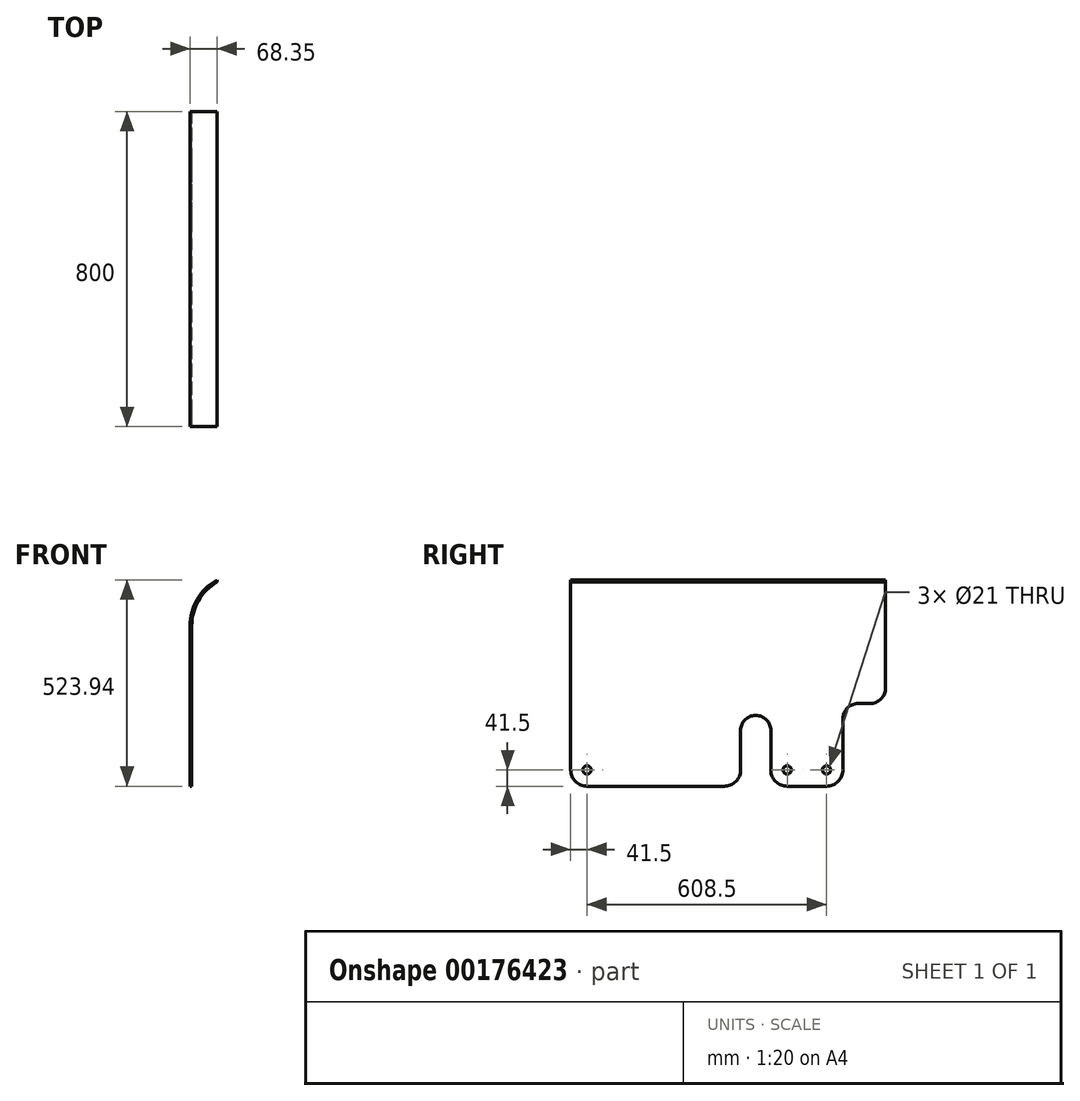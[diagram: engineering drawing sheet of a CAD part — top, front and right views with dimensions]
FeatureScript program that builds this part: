
annotation { "Feature Type Name" : "Feature", "Feature Type Description" : "" }
export const myFeature = defineFeature(function(context is Context, id is Id, definition is map)
    precondition{}
    {
        {
            var Q0;
            Q0=qCreatedBy(makeId("Front.planeOp"),FACE);
            var sketch = newSketch(context, id + "F0", { "sketchPlane" : qUnion([Q0])});
            skArc(sketch, "E0", {"start": v(68.35, 116.64) * mm, "mid": v(18.35, 67.6) * mm, "end": v(0, 0) * mm});
            skLineSegment(sketch, "E1", {"start": v(4.5, 0) * mm, "end": v(0, 0) * mm});
            skPoint(sketch, "E2", {"position": v(0, 0) * mm});
            skArc(sketch, "E3", {"start": v(68.35, 111.45) * mm, "mid": v(21.6, 64.22) * mm, "end": v(4.5, 0) * mm});
            skLineSegment(sketch, "E4", {"start": v(68.35, 116.64) * mm, "end": v(68.35, 111.45) * mm});
            skLineSegment(sketch, "E5.0", {"start": v(0, -365.8) * mm, "end": v(0, 0) * mm});
            skLineSegment(sketch, "E6", {"start": v(0, 0) * mm, "end": v(0, -407.3) * mm});
            skLineSegment(sketch, "E7", {"start": v(4.5, 0) * mm, "end": v(4.5, -407.3) * mm});
            skLineSegment(sketch, "E8", {"start": v(4.5, -407.3) * mm, "end": v(0, -407.3) * mm});
            skSolve(sketch);
        }
        {
            var Q0;
            Q0=qCreatedBy(makeId("Right.planeOp"),FACE);
            var sketch = newSketch(context, id + "F1", { "sketchPlane" : qUnion([Q0])});
            skLineSegment(sketch, "E9", {"start": v(0, 0) * mm, "end": v(800, 0) * mm});
            skLineSegment(sketch, "E10", {"start": v(800, 0) * mm, "end": v(800, -157.3) * mm});
            skLineSegment(sketch, "E11", {"start": v(760, -197.3) * mm, "end": v(730, -197.3) * mm});
            skLineSegment(sketch, "E12", {"start": v(691.5, -235.8) * mm, "end": v(691.5, -365.8) * mm});
            skLineSegment(sketch, "E13", {"start": v(650, -407.3) * mm, "end": v(550, -407.3) * mm});
            skLineSegment(sketch, "E14", {"start": v(508.5, -365.8) * mm, "end": v(508.5, -265.8) * mm});
            skLineSegment(sketch, "E15", {"start": v(431.5, -265.8) * mm, "end": v(431.5, -365.8) * mm});
            skLineSegment(sketch, "E16", {"start": v(390, -407.3) * mm, "end": v(41.5, -407.3) * mm});
            skLineSegment(sketch, "E17", {"start": v(0, -365.8) * mm, "end": v(0, 0) * mm});
            skPoint(sketch, "E18.visualSharp", {"position": v(0, -407.3) * mm});
            skArc(sketch, "E18.filletArc", {"start": v(0, -365.8) * mm, "mid": v(12.16, -395.14) * mm, "end": v(41.5, -407.3) * mm});
            skPoint(sketch, "E19.visualSharp", {"position": v(431.5, -407.3) * mm});
            skArc(sketch, "E19.filletArc", {"start": v(390, -407.3) * mm, "mid": v(419.34, -395.14) * mm, "end": v(431.5, -365.8) * mm});
            skPoint(sketch, "E20.visualSharp", {"position": v(508.5, -407.3) * mm});
            skArc(sketch, "E20.filletArc", {"start": v(508.5, -365.8) * mm, "mid": v(520.66, -395.14) * mm, "end": v(550, -407.3) * mm});
            skPoint(sketch, "E21.visualSharp", {"position": v(691.5, -407.3) * mm});
            skArc(sketch, "E21.filletArc", {"start": v(650, -407.3) * mm, "mid": v(679.34, -395.14) * mm, "end": v(691.5, -365.8) * mm});
            skPoint(sketch, "E22.visualSharp", {"position": v(691.5, -197.3) * mm});
            skArc(sketch, "E22.filletArc", {"start": v(730, -197.3) * mm, "mid": v(702.78, -208.58) * mm, "end": v(691.5, -235.8) * mm});
            skPoint(sketch, "E23.visualSharp", {"position": v(800, -197.3) * mm});
            skArc(sketch, "E23.filletArc", {"start": v(760, -197.3) * mm, "mid": v(788.28, -185.58) * mm, "end": v(800, -157.3) * mm});
            skArc(sketch, "E24", {"start": v(508.5, -265.8) * mm, "mid": v(470, -227.3) * mm, "end": v(431.5, -265.8) * mm});
            skCircle(sketch, "E25", {"center": v(41.5, -365.8) * mm, "radius": 10.5 * mm});
            skCircle(sketch, "E26", {"center": v(550, -365.8) * mm, "radius": 10.5 * mm});
            skCircle(sketch, "E27", {"center": v(650, -365.8) * mm, "radius": 10.5 * mm});
            skLineSegment(sketch, "E28", {"start": v(600, -135.8) * mm, "end": v(600, -155.8) * mm});
            skArc(sketch, "E29.0.startCap", {"start": v(589.5, -135.8) * mm, "mid": v(600, -125.3) * mm, "end": v(610.5, -135.8) * mm});
            skArc(sketch, "E29.0.endCap", {"start": v(610.5, -155.8) * mm, "mid": v(600, -166.3) * mm, "end": v(589.5, -155.8) * mm});
            skLineSegment(sketch, "E29.0.left", {"start": v(610.5, -135.8) * mm, "end": v(610.5, -155.8) * mm});
            skLineSegment(sketch, "E29.0.right", {"start": v(589.5, -135.8) * mm, "end": v(589.5, -155.8) * mm});
            skLineSegment(sketch, "E30", {"start": v(770, -115.8) * mm, "end": v(770, -155.8) * mm});
            skArc(sketch, "E31.0.startCap", {"start": v(759.5, -115.8) * mm, "mid": v(770, -105.3) * mm, "end": v(780.5, -115.8) * mm});
            skArc(sketch, "E31.0.endCap", {"start": v(780.5, -155.8) * mm, "mid": v(770, -166.3) * mm, "end": v(759.5, -155.8) * mm});
            skLineSegment(sketch, "E31.0.left", {"start": v(780.5, -115.8) * mm, "end": v(780.5, -155.8) * mm});
            skLineSegment(sketch, "E31.0.right", {"start": v(759.5, -115.8) * mm, "end": v(759.5, -155.8) * mm});
            skLineSegment(sketch, "E32", {"start": v(800, -157.3) * mm, "end": v(800, -407.3) * mm});
            skLineSegment(sketch, "E33", {"start": v(800, -407.3) * mm, "end": v(650, -407.3) * mm});
            skLineSegment(sketch, "E34", {"start": v(550, -407.3) * mm, "end": v(390, -407.3) * mm});
            skLineSegment(sketch, "E35", {"start": v(41.5, -407.3) * mm, "end": v(0, -407.3) * mm});
            skLineSegment(sketch, "E36", {"start": v(0, -365.8) * mm, "end": v(0, -407.3) * mm});
            skLineSegment(sketch, "E37", {"start": v(800, 116.64) * mm, "end": v(0, 116.64) * mm});
            skLineSegment(sketch, "E38", {"start": v(0, 111.45) * mm, "end": v(800, 111.45) * mm});
            skLineSegment(sketch, "E39", {"start": v(0, 0) * mm, "end": v(0, 116.64) * mm});
            skLineSegment(sketch, "E40", {"start": v(800, 116.64) * mm, "end": v(800, 0) * mm});
            skSolve(sketch);
        }
        {
            var Q0;
            Q0 = qSketchRegion(id + "F0", true);
            extrude(context, id + "F2", {"entities" : qUnion([Q0]), "oppositeDirection" : true, "depth" : 800 * mm});
        }
        {
            var Q0;
            Q0=makeQuery(id+"F1.imprint","IMPRINT",FACE,{"disambiguationData":[TD([[makeQuery(id+"F1.imprint","IMPRINT",EDGE,{"derivedFrom":sQuery(id+"F1.wireOp",EDGE,"E14")}),1.0]])]});
            var Q1;
            Q1=makeQuery(id+"F1.imprint","IMPRINT",FACE,{"disambiguationData":[TD([[makeQuery(id+"F1.imprint","IMPRINT",EDGE,{"derivedFrom":sQuery(id+"F1.wireOp",EDGE,"E11")}),1.0]])]});
            var Q2;
            Q2=makeQuery(id+"F1.imprint","IMPRINT",FACE,{"disambiguationData":[TD([[makeQuery(id+"F1.imprint","IMPRINT",EDGE,{"derivedFrom":sQuery(id+"F1.wireOp",EDGE,"E18.filletArc")}),-1.0]])]});
            var Q3;
            Q3=makeQuery(id+"F1.imprint","IMPRINT",FACE,{"disambiguationData":[TD([[makeQuery(id+"F1.imprint","IMPRINT",EDGE,{"derivedFrom":sQuery(id+"F1.wireOp",EDGE,"E25")}),1.0]])]});
            var Q4;
            Q4=makeQuery(id+"F1.imprint","IMPRINT",FACE,{"disambiguationData":[TD([[makeQuery(id+"F1.imprint","IMPRINT",EDGE,{"derivedFrom":sQuery(id+"F1.wireOp",EDGE,"E31.0.startCap")}),-1.0]])]});
            var Q5;
            Q5=makeQuery(id+"F1.imprint","IMPRINT",FACE,{"disambiguationData":[TD([[makeQuery(id+"F1.imprint","IMPRINT",EDGE,{"derivedFrom":sQuery(id+"F1.wireOp",EDGE,"E29.0.startCap")}),-1.0]])]});
            var Q6;
            Q6=makeQuery(id+"F1.imprint","IMPRINT",FACE,{"disambiguationData":[TD([[makeQuery(id+"F1.imprint","IMPRINT",EDGE,{"derivedFrom":sQuery(id+"F1.wireOp",EDGE,"E27")}),1.0]])]});
            var Q7;
            Q7=makeQuery(id+"F1.imprint","IMPRINT",FACE,{"disambiguationData":[TD([[makeQuery(id+"F1.imprint","IMPRINT",EDGE,{"derivedFrom":sQuery(id+"F1.wireOp",EDGE,"E26")}),1.0]])]});
            extrude(context, id + "F3", {"entities" : qUnion([Q0, Q1, Q2, Q3, Q4, Q5, Q6, Q7]), "operationType" : NewBodyOperationType.REMOVE, "depth" : 25 * mm});
        }
    });
